# Revit family: Холодильные шкафы из нержавеющей стали
name_source: partatom
category: Оборудование
units: mm (PartAtom-declared; Revit-internal decimal feet)

## family parameters
Всегда вертикально = Да
Классификация = Нет
На основе рабочей плоскости = Нет
Общий = Нет
При загрузке вырезать с полостями = Нет
Размер круглого соединителя = Использовать диаметр
Тип детали = Нормальный
Точка расчета площади = Нет

## types (20) — shared parameters
Допустимая нагрузка на полку, кг = 40
Замок = +
Клапан Шредера = +
Колесные опоры = опция
Расположение агрегата = верхнее
Система электропитания, В/Гц = 230/50
Тип охлаждения = динамический
Условия окр. среды (темп./влажн.) = до +40/до 80
Холодильный шкаф = <По категории>
zero-valued in all types: Отметка по умолчанию

## per-type parameters (varying)
- CM105-Gm: 1 дверь S=Нет; 1 дверь S (шир)=Нет; 1 дверь Sm=Да; 1 дверь Sm (шир)=Нет; 2  дверь S (шир)=Нет; 2 дверь S=Нет; 2 дверь Sm=Нет; 2 дверь Sm (шир)=Нет; Вес нетто/брутто, кг=96/115; Высота=1960 мм; Габаритные размеры, мм=697*695*1960; Глубина=695 мм; Диап. рабочих темп.=0....+6; Кол-во полок=4; Материал обшивок корпуса изнутри=снержавеющая сталь; Материал обшивок корпуса снаружи=нержавещая сталь (кроме задней стенки); Микропереключатель=клавишный; Объем, л=500; Панель S=Нет; Панель Sm=Да; Педаль=+; Подсветка=светодиодная; Потребляемая мощность, Вт=350; Размер полки, мм=595х455; Размеры в упаковке, мм=790x744x2125; Расход электроэнергии за сутки, кВт/ч=3,5; Терморегулятор=многофункциональная контрольная панель; Тип оттайки=авт. с системой исп. конденсата; Хладагент=R134a; Цена, руб.=67 108; Ширина=697 мм
- CM107-Gm: 1 дверь S=Нет; 1 дверь S (шир)=Нет; 1 дверь Sm=Да; 1 дверь Sm (шир)=Нет; 2  дверь S (шир)=Нет; 2 дверь S=Нет; 2 дверь Sm=Нет; 2 дверь Sm (шир)=Нет; Вес нетто/брутто, кг=112/137; Высота=1960 мм; Габаритные размеры, мм=697*925*1960; Глубина=925 мм; Диап. рабочих темп.=0....+6; Кол-во полок=4; Материал обшивок корпуса изнутри=нержавеющая сталь; Материал обшивок корпуса снаружи=нержавеющая сталь (кроме задней стенки); Микропереключатель=клавишный; Объем, л=700; Панель S=Нет; Панель Sm=Да; Педаль=+; Подсветка=светодиодная; Потребляемая мощность, Вт=350; Размер полки, мм=530х650; Размеры в упаковке, мм=790x988x2125; Расход электроэнергии за сутки, кВт/ч=3,5; Терморегулятор=многофункциональная контрольная панель; Тип оттайки=авт. с системой исп. конденсата; Хладагент=R134a; Цена, руб.=73 495; Ширина=697 мм
- CV105-Gm: 1 дверь S=Нет; 1 дверь S (шир)=Нет; 1 дверь Sm=Да; 1 дверь Sm (шир)=Нет; 2  дверь S (шир)=Нет; 2 дверь S=Нет; 2 дверь Sm=Нет; 2 дверь Sm (шир)=Нет; Вес нетто/брутто, кг=96/115; Высота=1960 мм; Габаритные размеры, мм=697*695*1960; Глубина=695 мм; Диап. рабочих темп.=-5....+5; Кол-во полок=4; Материал обшивок корпуса изнутри=нержавеющая сталь; Материал обшивок корпуса снаружи=нержавеющая сталь (кроме задней стенки); Микропереключатель=клавишный; Объем, л=500; Панель S=Нет; Панель Sm=Да; Педаль=+; Подсветка=светодиодная; Потребляемая мощность, Вт=400; Размер полки, мм=595х455; Размеры в упаковке, мм=790x744x2125; Расход электроэнергии за сутки, кВт/ч=4; Терморегулятор=многофункциональная контрольная панель; Тип оттайки=авт. с системой исп. конденсата; Хладагент=R134a; Цена, руб.=71 085; Ширина=697 мм
- CV107-Gm: 1 дверь S=Нет; 1 дверь S (шир)=Нет; 1 дверь Sm=Да; 1 дверь Sm (шир)=Нет; 2  дверь S (шир)=Нет; 2 дверь S=Нет; 2 дверь Sm=Нет; 2 дверь Sm (шир)=Нет; Вес нетто/брутто, кг=114/139; Высота=1960 мм; Габаритные размеры, мм=697*925*1960; Глубина=925 мм; Диап. рабочих темп.=-5....+5; Кол-во полок=4; Материал обшивок корпуса изнутри=нержавеющая сталь; Материал обшивок корпуса снаружи=нержавеющая сталь (кроме задней стенки); Микропереключатель=клавишный; Объем, л=700; Панель S=Нет; Панель Sm=Да; Педаль=+; Подсветка=+; Потребляемая мощность, Вт=400; Размер полки, мм=530х650; Размеры в упаковке, мм=790x988x2125; Расход электроэнергии за сутки, кВт/ч=4,5; Терморегулятор=многофункциональная контрольная панель; Тип оттайки=авт. с системой исп. конденсата; Хладагент=R134a; Цена, руб.=80 136; Ширина=697 мм
- CB107-Gm: 1 дверь S=Нет; 1 дверь S (шир)=Нет; 1 дверь Sm=Нет; 1 дверь Sm (шир)=Да; 2  дверь S (шир)=Нет; 2 дверь S=Нет; 2 дверь Sm=Нет; 2 дверь Sm (шир)=Нет; Вес нетто/брутто, кг=128/152; Высота=1996 мм; Габаритные размеры, мм=735*960*1996; Глубина=960 мм; Диап. рабочих темп.=не выше -18; Кол-во полок=4; Материал обшивок корпуса изнутри=нержавеющая сталь; Материал обшивок корпуса снаружи=нержавеющая сталь (кроме задней стенки); Микропереключатель=клавишный; Объем, л=700; Панель S=Нет; Панель Sm=Да; Педаль=+; Подсветка=светодиодная; Потребляемая мощность, Вт=550/400; Размер полки, мм=530х650; Размеры в упаковке, мм=850x988x2125; Расход электроэнергии за сутки, кВт/ч=12; Терморегулятор=многофункциональная контрольная панель; Тип оттайки=авт. с системой исп. конденсата; Хладагент=R404А; Цена, руб.=85 322; Ширина=735 мм
- CM110-Gm: 1 дверь S=Нет; 1 дверь S (шир)=Нет; 1 дверь Sm=Да; 1 дверь Sm (шир)=Нет; 2  дверь S (шир)=Нет; 2 дверь S=Нет; 2 дверь Sm=Да; 2 дверь Sm (шир)=Нет; Вес нетто/брутто, кг=158/187; Высота=1960 мм; Габаритные размеры, мм=1402*695*1960; Глубина=695 мм; Диап. рабочих темп.=0....+6; Кол-во полок=8; Материал обшивок корпуса изнутри=нержавеющая сталь; Материал обшивок корпуса снаружи=нержавеющая сталь (кроме задней стенки); Микропереключатель=клавишный; Объем, л=1000; Панель S=Нет; Панель Sm=Да; Педаль=+; Подсветка=светодиодная; Потребляемая мощность, Вт=550; Размер полки, мм=595х455; Размеры в упаковке, мм=1490x744x2125; Расход электроэнергии за сутки, кВт/ч=5.5; Терморегулятор=многофункциональная контрольная панель; Тип оттайки=авт. с системой исп. конденсата; Хладагент=R134a; Цена, руб.=89 186; Ширина=1402 мм
- CM114-Gm: 1 дверь S=Нет; 1 дверь S (шир)=Нет; 1 дверь Sm=Да; 1 дверь Sm (шир)=Нет; 2  дверь S (шир)=Нет; 2 дверь S=Нет; 2 дверь Sm=Да; 2 дверь Sm (шир)=Нет; Вес нетто/брутто, кг=186/218; Высота=1960 мм; Габаритные размеры, мм=1402*925*1960; Глубина=925 мм; Диап. рабочих темп.=0....+6; Кол-во полок=8; Материал обшивок корпуса изнутри=нержавеющая сталь; Материал обшивок корпуса снаружи=нержавеющая сталь (кроме задней стенки); Микропереключатель=клавишный; Объем, л=1400; Панель S=Нет; Панель Sm=Да; Педаль=+; Подсветка=светодиодная; Потребляемая мощность, Вт=550; Размер полки, мм=530х650; Размеры в упаковке, мм=1490x988x2125; Расход электроэнергии за сутки, кВт/ч=6; Терморегулятор=многофункциональная контрольная панель; Тип оттайки=авт. с системой исп. конденсата; Хладагент=R134a; Цена, руб.=99 356; Ширина=1402 мм
- CV110-Gm: 1 дверь S=Нет; 1 дверь S (шир)=Нет; 1 дверь Sm=Да; 1 дверь Sm (шир)=Нет; 2  дверь S (шир)=Нет; 2 дверь S=Нет; 2 дверь Sm=Да; 2 дверь Sm (шир)=Нет; Вес нетто/брутто, кг=158/187; Высота=1960 мм; Габаритные размеры, мм=1402*695*1960; Глубина=695 мм; Диап. рабочих темп.=-5....+5; Кол-во полок=8; Материал обшивок корпуса изнутри=нержавеющая сталь; Материал обшивок корпуса снаружи=нержавеющая сталь (кроме задней стенки); Микропереключатель=клавишный; Объем, л=1000; Панель S=Нет; Панель Sm=Да; Педаль=+; Подсветка=светодиодная; Потребляемая мощность, Вт=630; Размер полки, мм=595х455; Размеры в упаковке, мм=1490x988x2125; Расход электроэнергии за сутки, кВт/ч=6; Терморегулятор=многофункциональная контрольная панель; Тип оттайки=авт. с системой исп. конденсата; Хладагент=R134a; Цена, руб.=103 932; Ширина=1402 мм
- CV114-Gm: 1 дверь S=Нет; 1 дверь S (шир)=Нет; 1 дверь Sm=Да; 1 дверь Sm (шир)=Нет; 2  дверь S (шир)=Нет; 2 дверь S=Нет; 2 дверь Sm=Да; 2 дверь Sm (шир)=Нет; Вес нетто/брутто, кг=168/218; Высота=1960 мм; Габаритные размеры, мм=1402*925*1960; Глубина=925 мм; Диап. рабочих темп.=-5....+5; Кол-во полок=8; Материал обшивок корпуса изнутри=нержавеющая сталь; Материал обшивок корпуса снаружи=нержавеющая сталь (кроме задней стенки); Микропереключатель=клавишный; Объем, л=1400; Панель S=Нет; Панель Sm=Да; Педаль=+; Подсветка=светодиодная; Потребляемая мощность, Вт=630; Размер полки, мм=530х650; Размеры в упаковке, мм=1490x988x2125; Расход электроэнергии за сутки, кВт/ч=6.5; Терморегулятор=многофункциональная контрольная панель; Тип оттайки=авт. с системой исп. конденсата; Хладагент=R134a; Цена, руб.=109 525; Ширина=1402 мм
- CM105-G: 1 дверь S=Да; 1 дверь S (шир)=Нет; 1 дверь Sm=Нет; 1 дверь Sm (шир)=Нет; 2  дверь S (шир)=Нет; 2 дверь S=Нет; 2 дверь Sm=Нет; 2 дверь Sm (шир)=Нет; Вес нетто/брутто, кг=96/115; Высота=1960 мм; Габаритные размеры, мм=697*695*1960; Глубина=695 мм; Диап. рабочих темп.=0....+6; Кол-во полок=4; Материал обшивок корпуса изнутри=нержавеющая сталь; Материал обшивок корпуса снаружи=нержавеющая сталь (кроме задней стенки); Микропереключатель=-; Объем, л=500; Панель S=Да; Панель Sm=Нет; Педаль=+; Подсветка=светодиоидная; Потребляемая мощность, Вт=350; Размер полки, мм=595х455; Размеры в упаковке, мм=790x744x2125; Расход электроэнергии за сутки, кВт/ч=3,5; Терморегулятор=эл. блок управления; Тип оттайки=авт.с системой исп. конденсата; Хладагент=R134a; Цена, руб.=67 108; Ширина=697 мм
- CM107-G: 1 дверь S=Да; 1 дверь S (шир)=Нет; 1 дверь Sm=Нет; 1 дверь Sm (шир)=Нет; 2  дверь S (шир)=Нет; 2 дверь S=Нет; 2 дверь Sm=Нет; 2 дверь Sm (шир)=Нет; Вес нетто/брутто, кг=114/139; Высота=1960 мм; Габаритные размеры, мм=697*925*1960; Глубина=925 мм; Диап. рабочих темп.=0....+6; Кол-во полок=4; Материал обшивок корпуса изнутри=нержавеющая сталь; Материал обшивок корпуса снаружи=нержавеющая сталь (кроме задней стенки); Объем, л=700; Панель S=Да; Панель Sm=Нет; Подсветка=светодиодная; Потребляемая мощность, Вт=350; Размер полки, мм=530х650; Размеры в упаковке, мм=790x988x2125; Расход электроэнергии за сутки, кВт/ч=4; Терморегулятор=эл. блок управления; Тип оттайки=авт. с системой исп. конденсата; Хладагент=R134a; Цена, руб.=73 495; Ширина=697 мм
- CM110-G: 1 дверь S=Да; 1 дверь S (шир)=Нет; 1 дверь Sm=Нет; 1 дверь Sm (шир)=Нет; 2  дверь S (шир)=Нет; 2 дверь S=Да; 2 дверь Sm=Нет; 2 дверь Sm (шир)=Нет; Вес нетто/брутто, кг=155/187; Высота=1960 мм; Габаритные размеры, мм=1402*695*1960; Глубина=695 мм; Диап. рабочих темп.=0....+6; Кол-во полок=8; Материал обшивок корпуса изнутри=нержавеющая сталь; Материал обшивок корпуса снаружи=нержавеющая сталь (кроме задней стенки); Объем, л=1000; Панель S=Да; Панель Sm=Нет; Подсветка=светодиодная; Потребляемая мощность, Вт=550; Размер полки, мм=595х455; Размеры в упаковке, мм=1490x744x2125; Расход электроэнергии за сутки, кВт/ч=5.5; Терморегулятор=эл. блок управления; Тип оттайки=авт. с системой исп. конденсата; Хладагент=R134a; Цена, руб.=89 186; Ширина=1402 мм
- CB114-Gm: 1 дверь S=Нет; 1 дверь S (шир)=Нет; 1 дверь Sm=Нет; 1 дверь Sm (шир)=Да; 2  дверь S (шир)=Нет; 2 дверь S=Нет; 2 дверь Sm=Нет; 2 дверь Sm (шир)=Да; Вес нетто/брутто, кг=217/247; Высота=1996 мм; Габаритные размеры, мм=1474*960*1996; Глубина=960 мм; Диап. рабочих темп.=не выше -18; Кол-во полок=4; Материал обшивок корпуса изнутри=нержавеющая сталь; Материал обшивок корпуса снаружи=нержавеющая сталь (кроме задней стенки); Микропереключатель=клавишный; Объем, л=1400; Панель S=Нет; Панель Sm=Да; Педаль=+; Подсветка=светодиодная; Потребляемая мощность, Вт=800/1200; Размер полки, мм=530х650; Размеры в упаковке, мм=1550x988x2160; Расход электроэнергии за сутки, кВт/ч=20.5; Терморегулятор=многофункциональная контрольная панель; Тип оттайки=авт. с системой исп. конденсата; Хладагент=R404А; Цена, руб.=121 932; Ширина=1474 мм
- CB107-G: 1 дверь S=Нет; 1 дверь S (шир)=Да; 1 дверь Sm=Нет; 1 дверь Sm (шир)=Нет; 2  дверь S (шир)=Нет; 2 дверь S=Нет; 2 дверь Sm=Нет; 2 дверь Sm (шир)=Нет; Вес нетто/брутто, кг=114/139; Высота=1996 мм; Габаритные размеры, мм=735*960*1996; Глубина=960 мм; Диап. рабочих темп.=не выше -18; Кол-во полок=4; Материал обшивок корпуса изнутри=нержавеющая сталь; Материал обшивок корпуса снаружи=нержавеющая сталь (кроме задней стенки); Объем, л=700; Панель S=Да; Панель Sm=Нет; Подсветка=светодиодная; Потребляемая мощность, Вт=550/400; Размер полки, мм=530х650; Размеры в упаковке, мм=850x988x2160; Расход электроэнергии за сутки, кВт/ч=12; Терморегулятор=эл. блок управления; Тип оттайки=автоматическая; Хладагент=R134a; Цена, руб.=85 322; Ширина=735 мм
- CV105-G: 1 дверь S=Да; 1 дверь S (шир)=Нет; 1 дверь Sm=Нет; 1 дверь Sm (шир)=Нет; 2  дверь S (шир)=Нет; 2 дверь S=Нет; 2 дверь Sm=Нет; 2 дверь Sm (шир)=Нет; Вес нетто/брутто, кг=96/115; Высота=1960 мм; Габаритные размеры, мм=697*695*1960; Глубина=695 мм; Диап. рабочих темп.=-5....+5; Кол-во полок=4; Материал обшивок корпуса изнутри=нержавеющая сталь; Материал обшивок корпуса снаружи=нержавеющая сталь (кроме задней стенки); Объем, л=500; Панель S=Да; Панель Sm=Нет; Подсветка=светодиодная; Потребляемая мощность, Вт=400; Размер полки, мм=595х455; Размеры в упаковке, мм=790x744x2125; Расход электроэнергии за сутки, кВт/ч=4; Терморегулятор=эл. блок управления; Тип оттайки=авт. с системой исп. конденсата; Хладагент=R134a; Цена, руб.=71 085; Ширина=697 мм
- CV107-G: 1 дверь S=Да; 1 дверь S (шир)=Нет; 1 дверь Sm=Нет; 1 дверь Sm (шир)=Нет; 2  дверь S (шир)=Нет; 2 дверь S=Нет; 2 дверь Sm=Нет; 2 дверь Sm (шир)=Нет; Вес нетто/брутто, кг=114/139; Высота=1960 мм; Габаритные размеры, мм=697*925*1960; Глубина=925 мм; Диап. рабочих темп.=-5....+5; Кол-во полок=4; Материал обшивок корпуса изнутри=нержавеющая сталь; Материал обшивок корпуса снаружи=нержавеющая сталь (кроме задней стенки); Объем, л=700; Панель S=Да; Панель Sm=Нет; Подсветка=светодиодная; Потребляемая мощность, Вт=400; Размер полки, мм=530х650; Размеры в упаковке, мм=790x988x2125; Расход электроэнергии за сутки, кВт/ч=4,5; Терморегулятор=многофункциональная контрольная панель; Тип оттайки=авт. с системой исп. конденсата; Хладагент=R134a; Цена, руб.=80 136; Ширина=697 мм
- CV110-G: 1 дверь S=Да; 1 дверь S (шир)=Нет; 1 дверь Sm=Нет; 1 дверь Sm (шир)=Нет; 2  дверь S (шир)=Нет; 2 дверь S=Да; 2 дверь Sm=Нет; 2 дверь Sm (шир)=Нет; Вес нетто/брутто, кг=158/187; Высота=1960 мм; Габаритные размеры, мм=1402*695*1960; Глубина=695 мм; Диап. рабочих темп.=-5....+5; Кол-во полок=8; Материал обшивок корпуса изнутри=нержавеющая сталь; Материал обшивок корпуса снаружи=нержавеющая сталь (кроме задней стенки); Объем, л=1000; Панель S=Да; Панель Sm=Нет; Подсветка=светодиодная; Потребляемая мощность, Вт=630; Размер полки, мм=595х455; Размеры в упаковке, мм=1490x988x2125; Расход электроэнергии за сутки, кВт/ч=6; Терморегулятор=многофункциональная контрольная панель; Тип оттайки=авт. с системой исп. конденсата; Хладагент=R134a; Цена, руб.=103 932; Ширина=1402 мм
- CV114-G: 1 дверь S=Да; 1 дверь S (шир)=Нет; 1 дверь Sm=Нет; 1 дверь Sm (шир)=Нет; 2  дверь S (шир)=Нет; 2 дверь S=Да; 2 дверь Sm=Нет; 2 дверь Sm (шир)=Нет; Вес нетто/брутто, кг=168/218; Высота=1960 мм; Габаритные размеры, мм=1402*925*1960; Глубина=925 мм; Диап. рабочих темп.=-5....+5; Кол-во полок=8; Материал обшивок корпуса изнутри=нержавеющая сталь; Материал обшивок корпуса снаружи=нержавеющая сталь (кроме задней стенки); Объем, л=1400; Панель S=Да; Панель Sm=Нет; Подсветка=светодиодная; Потребляемая мощность, Вт=630; Размер полки, мм=530х650; Размеры в упаковке, мм=1490x988x2125; Расход электроэнергии за сутки, кВт/ч=6.5; Терморегулятор=эл. блок управления; Тип оттайки=авт., при помощи ТЭНов, с системой исп. конденсата; Хладагент=R134a; Цена, руб.=109 525; Ширина=1402 мм
- CB114-G: 1 дверь S=Нет; 1 дверь S (шир)=Да; 1 дверь Sm=Нет; 1 дверь Sm (шир)=Нет; 2  дверь S (шир)=Да; 2 дверь S=Нет; 2 дверь Sm=Нет; 2 дверь Sm (шир)=Нет; Вес нетто/брутто, кг=168/218; Высота=1996 мм; Габаритные размеры, мм=1474*960*1996; Глубина=960 мм; Диап. рабочих темп.=не выше -18; Кол-во полок=4; Материал обшивок корпуса изнутри=нержавеющая сталь; Материал обшивок корпуса снаружи=нержавеющая сталь (кроме задней стенки); Объем, л=1400; Панель S=Да; Панель Sm=Нет; Подсветка=светодиодная; Потребляемая мощность, Вт=800/1200; Размер полки, мм=530х650; Размеры в упаковке, мм=1550x988x2160; Расход электроэнергии за сутки, кВт/ч=20.5; Терморегулятор=эл. блок управления; Тип оттайки=автоматическая; Хладагент=R404А; Цена, руб.=121 932; Ширина=1474 мм
- CM114-G: 1 дверь S=Да; 1 дверь S (шир)=Нет; 1 дверь Sm=Нет; 1 дверь Sm (шир)=Нет; 2  дверь S (шир)=Нет; 2 дверь S=Да; 2 дверь Sm=Нет; 2 дверь Sm (шир)=Нет; Вес нетто/брутто, кг=186/218; Высота=1960 мм; Габаритные размеры, мм=1402*925*1960; Глубина=925 мм; Диап. рабочих темп.=0....+6; Кол-во полок=8; Материал обшивок корпуса изнутри=нержавеющая сталь; Материал обшивок корпуса снаружи=нержавеющая сталь (кроме задней стенки); Объем, л=1400; Панель S=Да; Панель Sm=Нет; Подсветка=светодиодная; Потребляемая мощность, Вт=550; Размер полки, мм=530х650; Размеры в упаковке, мм=1490x988x2125; Расход электроэнергии за сутки, кВт/ч=6; Терморегулятор=эл. блок управления; Тип оттайки=авт. с системой исп. конденсата; Хладагент=R134a; Цена, руб.=99 356; Ширина=1402 мм
